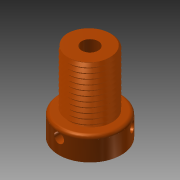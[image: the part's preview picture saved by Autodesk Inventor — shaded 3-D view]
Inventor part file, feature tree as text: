
AUTODESK INVENTOR PART (.ipt)
format: ipt  version: 2013 (Build 170138000, 138)  size: 358,912 bytes
history: native  units: mm
features: sketch x8, extrude x7, helix x1, pattern_circular x1, fillet x1, projected_geometry x1
ambient origin geometry x8: Origin, YZ Plane, XZ Plane, XY Plane, X Axis, Y Axis, Z Axis, Center Point
bodies: Solid1 (feature_tree)
feature tree (19):
  extrude  "Extrusion1"  Depth=17.0mm TaperAngle=0.0deg
  extrude  "Extrusion2"  Depth=1.5mm
  helix  "Coil1"  [1 undecoded]
  extrude  "Extrusion7"  Depth=5.0mm
  extrude  "Extrusion3"  Depth=10.0mm TaperAngle=0.0deg
  extrude  "Extrusion4"  Depth=5.0mm
  extrude  "Extrusion9"  Depth=2.5mm
  pattern_circular  "Circular Pattern1"  Count=3 Angle=360.0deg
  fillet  "Fillet1"  Radius=1.0mm
  extrude  "Extrusion10"  Depth=2.0mm TaperAngle=0.0deg
  sketch  "Sketch1"  dims[d0=12.0mm d2=17.0mm d3=0.0mm]
  sketch  "Sketch2"  dims[d5=5.0mm d6=0.0mm d7=1.5mm]
  sketch  "Sketch3"  dims[d8=1.501mm d9=10.0mm d10=150.0mm d11=0.0mm d12=90.0deg d13=90.0deg d14=0.0mm d15=0.0mm d19=40.0mm]
  sketch  "Sketch4"  dims[d21=100.0mm d22=0.0mm d23=5.0mm]
  sketch  "Sketch5"  dims[d26=100.0mm d27=0.0mm d45=10.0mm d46=0.0mm]
  sketch  "Sketch8"  dims[d51=7.0mm d52=5.0mm]
  sketch  "Sketch9"  dims[d54=3.0mm d56=2.5mm]
  sketch  "Sketch10"  dims[d57=10.0mm d58=0.0mm d59=30.0mm d60=360.0deg d62=1.0mm d63=2.0mm d64=0.0mm]
  projected_geometry  "Project Cut Edges1"
note: 1 required parameter value undecoded (feature->parameter linkage not recoverable at this tier; creation-order binding heuristic only, values carry confidence <= 0.55)
